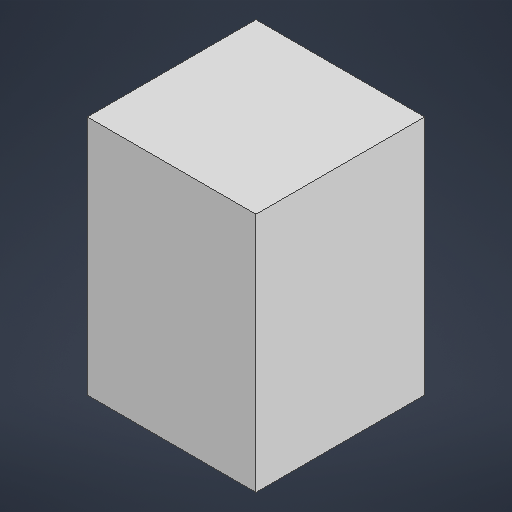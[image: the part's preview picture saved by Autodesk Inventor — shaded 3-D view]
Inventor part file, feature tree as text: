
AUTODESK INVENTOR PART (.ipt)
format: ipt  version: 2025.2 (Build 292293000, 293)  size: 147,456 bytes
history: native  units: mm
features: extrude x1, sketch x1
ambient origin geometry x8: Origin, YZ Plane, XZ Plane, XY Plane, X Axis, Y Axis, Z Axis, Center Point
bodies: Solid1 (feature_tree)
feature tree (2):
  extrude  "Extrusion1"  Depth=14.0mm
  sketch  "Sketch1"  dims[d0=14.0mm d1=14.0mm d2=20.0mm d3=0.0mm]
